# Revit family: Sanitary_Taps&Mixers_Zurn_Z86100-XL
name_source: partatom
category: Plumbing Fixtures
units: mm (PartAtom-declared; Revit-internal decimal feet)

## family parameters
Cut with Voids When Loaded = No
Host = Face
Maintain Annotation Orientation = No
OmniClass Number = 23.45.55.17
OmniClass Title = Mixing Faucets
Part Type = Normal
Room Calculation Point = No
Round Connector Dimension = Use Radius
Shared = No

## types (6) — shared parameters
Assembly Code = D2010.60
CW Connection = Yes
CWFU = 1
Default Elevation = 34 "
Description = Single Basin, Metering Faucet (Lead Free)
Distance B/W Base & Aerator = 3.75 "
HW Connection = Yes
Inlet Connection Size (inch) = 0.5 "
Manufacturer = Zurn Industries, LLC
Manufacturer Brand = Zurn
Model = Z86100-XL
Modified date = 08/29/2025
Product Documentation Link = https://files.zurn.com
Product Installation Sheet URL = https://files.zurn.com
Product Page URL = https://www.zurn.com
Product data url = https://www.bimobject.com
Repair Parts URL = https://files.zurn.com
Spout Base Width = 1.875 "
Spout Reach = 1.375 "
URL = http://www.zurn.com
Vent Connection = No
Waste Connection = No
zero-valued in all types: HWFU, WFU

## per-type parameters (varying)
| type | Flow Rate | Main Material | Type of Outlet |
| Z86100-XL-3M (0.5 GPM SPRAY OUTLET) | 1 GPM | Brass_Zurn_ Chrome Polished | SPRAY |
| Z86100-XL-7M (1.0 GPM SPRAY OUTLET) | 1 GPM | Chrome-Plated Brass - Zurn - Polished | SPRAY |
| Z86100-XL-16M (1.0 GPM SPRAY OUTLET) | 1 GPM | Brass_Zurn_ Chrome Polished | SPRAY |
| Z86100-XL-22M (1.0 GPM LAMINAR OUTLET) | 1 GPM | Brass_Zurn_ Chrome Polished | LAMINAR |
| Z86100-XL-25M (0.35 GPM SPRAY OUTLET) | 0 GPM | Brass_Zurn_ Chrome Polished | SPRAY |
| Z86100-XL-28M (0.5 GPM LAMINAR OUTLET) | 1 GPM | Brass_Zurn_ Chrome Polished | LAMINAR |

## geometry (parser evidence)
native form markers: Sweep x4
no freeform markers — native parametric forms only
